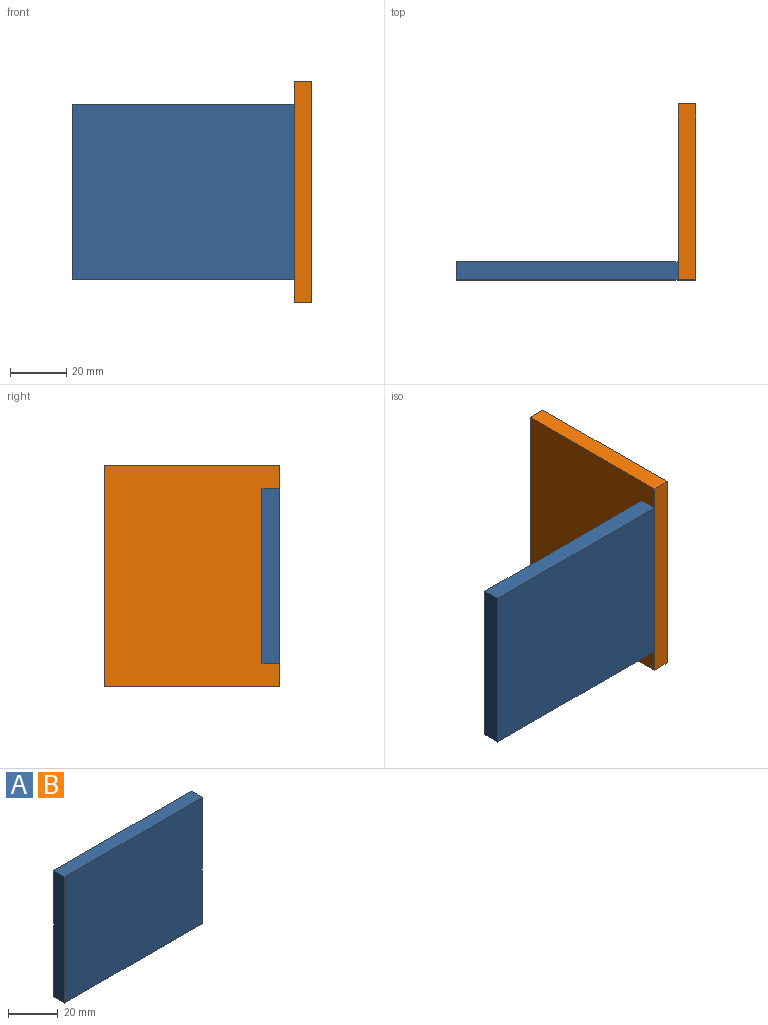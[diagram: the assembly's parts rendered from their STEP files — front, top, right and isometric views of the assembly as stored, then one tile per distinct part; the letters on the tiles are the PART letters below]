
ASSEMBLY  parts=2 mates=3
PART A: 6 faces, bbox 78.6x6.4x62.2 mm
  f0: plane 78.62x6.35mm, normal (0,0,-1), area 499.2mm2, adj f1,f3,f4,f5
  f1: plane 62.25x6.35mm, normal (1,0,0), area 395.3mm2, adj f0,f2,f4,f5
  f2: plane 78.62x6.35mm, normal (0,0,1), area 499.2mm2, adj f1,f3,f4,f5
  f3: plane 62.25x6.35mm, normal (-1,0,0), area 395.3mm2, adj f0,f2,f4,f5
  f4: plane 78.62x62.25mm, normal (0,-1,0), area 4893.8mm2, adj f0,f1,f2,f3
  f5: plane 78.62x62.25mm, normal (0,1,0), area 4893.8mm2, adj f0,f1,f2,f3
PART B: same geometry as A
PLACE A t=(46.81,-39.54,25.57)mm
PLACE B rot(axis=(-0.58,0.58,0.58),120deg) t=(102.81,-14.76,42.26)mm
MATE planar A.f4 <-> B.f0  axis (0,-1,0) through (63.5,-45.89,25.57)mm
MATE parallel B.f4 <-> A.f1  axis (1,0,0) through (109.16,-14.76,25.57)mm
MATE planar A.f1 <-> B.f5  axis (1,0,0) through (102.81,-39.54,25.57)mm
